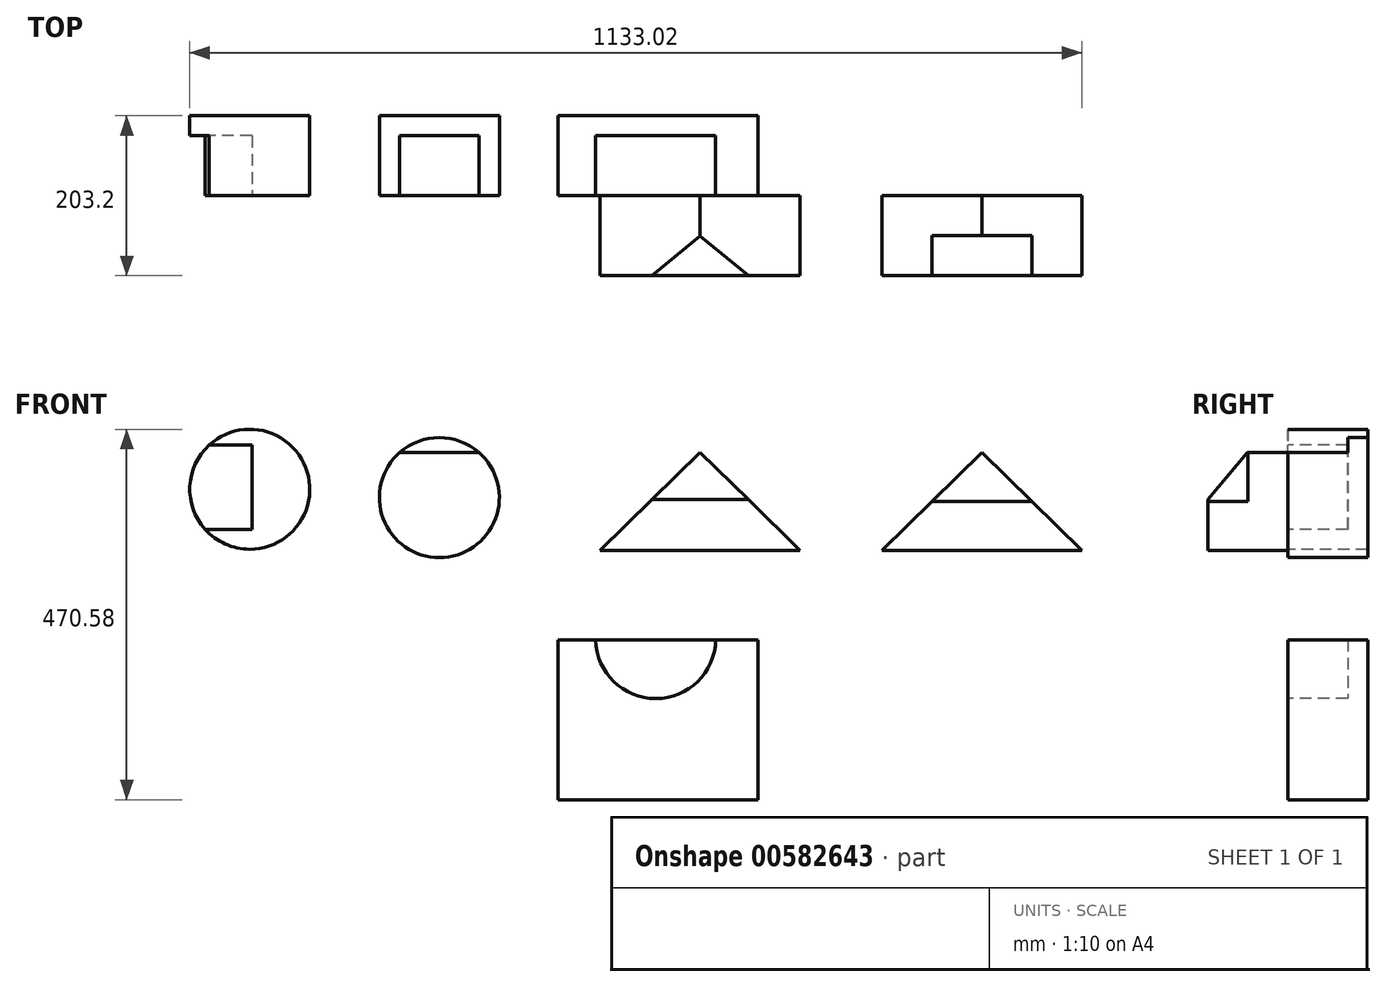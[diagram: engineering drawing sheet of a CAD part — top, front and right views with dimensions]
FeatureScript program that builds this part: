
annotation { "Feature Type Name" : "Feature", "Feature Type Description" : "" }
export const myFeature = defineFeature(function(context is Context, id is Id, definition is map)
    precondition{}
    {
        {
            var Q0;
            Q0=qCreatedBy(makeId("Front.planeOp"),FACE);
            var sketch = newSketch(context, id + "F0", { "sketchPlane" : qUnion([Q0])});
            skLineSegment(sketch, "E0", {"start": v(0, 0) * mm, "end": v(254, 0) * mm});
            skLineSegment(sketch, "E1", {"start": v(254, 0) * mm, "end": v(127, 124.43) * mm});
            skLineSegment(sketch, "E2", {"start": v(127, 124.43) * mm, "end": v(0, 0) * mm});
            skLineSegment(sketch, "E3", {"start": v(190.5, 62.22) * mm, "end": v(63.5, 62.22) * mm});
            skSolve(sketch);
        }
        {
            var Q0;
            {var subQ0=sQuery(id+"F0.wireOp",EDGE,"E0");Q0=makeQuery(id+"F0.imprint","IMPRINT",FACE,{"disambiguationData":[TD([[makeQuery(id+"F0.imprint","IMPRINT",EDGE,{"derivedFrom":subQ0}),1.0]])]});}
            extrude(context, id + "F1", {"entities" : qUnion([Q0]), "depth" : 101.6 * mm, "offsetDistance" : 25.4 * mm});
        }
        {
            var Q0;
            Q0 = qSketchRegion(id + "F0", true);
            extrude(context, id + "F2", {"entities" : qUnion([Q0]), "operationType" : NewBodyOperationType.ADD, "depth" : 50.8 * mm, "offsetDistance" : 25.4 * mm});
        }
        {
            var Q0;
            Q0=qCreatedBy(makeId("Front.planeOp"),FACE);
            var sketch = newSketch(context, id + "F3", { "sketchPlane" : qUnion([Q0])});
            skLineSegment(sketch, "E4", {"start": v(-103.68, 0) * mm, "end": v(-357.68, 0) * mm});
            skLineSegment(sketch, "E5", {"start": v(-357.68, 0) * mm, "end": v(-230.68, 124.43) * mm});
            skLineSegment(sketch, "E6", {"start": v(-230.68, 124.43) * mm, "end": v(-103.68, 0) * mm});
            skSolve(sketch);
        }
        {
            var Q0;
            Q0=makeQuery(id+"F3.imprint","IMPRINT",FACE,{"disambiguationData":[TD([[makeQuery(id+"F3.imprint","IMPRINT",EDGE,{"derivedFrom":sQuery(id+"F3.wireOp",EDGE,"E4")}),-1.0]])]});
            extrude(context, id + "F4", {"entities" : qUnion([Q0]), "depth" : 101.6 * mm, "offsetDistance" : 25.4 * mm});
        }
        {
            var Q0;
            Q0=makeQuery(id+"F4.opExtrude","CAP_EDGE",EDGE,{"disambiguationData":[OSD([sQuery(id+"F3.wireOp",EDGE,"E4")])],"isStart":false});
            cPoint(context, id + "F5", {"entities" : qUnion([Q0]), "parameter" : 0.5});
        }
        {
            var Q0;
            Q0=makeQuery(id+"F4.opExtrude","CAP_VERTEX",VERTEX,{"disambiguationData":[OSD([sQuery(id+"F3.wireOp",EDGE,"E5"),sQuery(id+"F3.wireOp",EDGE,"E6")])],"isStart":false});
            var Q1;
            Q1=makeQuery(id+"F4.opExtrude","CAP_VERTEX",VERTEX,{"disambiguationData":[OSD([sQuery(id+"F3.wireOp",EDGE,"E5"),sQuery(id+"F3.wireOp",EDGE,"E6")])],"isStart":true});
            var Q2;
            Q2 = qCreatedBy(id + "F5" ,VERTEX);
            cPlane(context, id + "F6", {"entities" : qUnion([Q0, Q1, Q2]), "cplaneType" : CPlaneType.THREE_POINT, "offset" : 25.4 * mm, "width" : 152.4 * mm, "height" : 152.4 * mm});
        }
        {
            var Q0;
            Q0=qCreatedBy(id+"F6.planeOp",FACE);
            var sketch = newSketch(context, id + "F7", { "sketchPlane" : qUnion([Q0])});
            skLineSegment(sketch, "E7", {"start": v(-51.02, 124.47) * mm, "end": v(-101.82, 124.47) * mm});
            skLineSegment(sketch, "E8", {"start": v(-101.82, 124.47) * mm, "end": v(-101.82, 64.04) * mm});
            skLineSegment(sketch, "E9", {"start": v(-101.82, 64.04) * mm, "end": v(-51.02, 124.47) * mm});
            skSolve(sketch);
        }
        {
            var Q0;
            Q0 = qSketchRegion(id + "F7", true);
            extrude(context, id + "F8", {"entities" : qUnion([Q0]), "operationType" : NewBodyOperationType.REMOVE, "endBound" : BoundingType.SYMMETRIC, "depth" : 127 * mm, "offsetDistance" : 25.4 * mm});
        }
        {
            var Q0;
            Q0=qCreatedBy(makeId("Front.planeOp"),FACE);
            var sketch = newSketch(context, id + "F9", { "sketchPlane" : qUnion([Q0])});
            skCircle(sketch, "E10", {"center": v(-562.02, 67) * mm, "radius": 76.2 * mm});
            skSolve(sketch);
        }
        {
            var Q0;
            Q0=makeQuery(id+"F9.imprint","IMPRINT",FACE,{"disambiguationData":[TD([[makeQuery(id+"F9.imprint","IMPRINT",EDGE,{"derivedFrom":sQuery(id+"F9.wireOp",EDGE,"E10")}),1.0]])]});
            extrude(context, id + "F10", {"entities" : qUnion([Q0]), "oppositeDirection" : true, "depth" : 101.6 * mm, "offsetDistance" : 25.4 * mm});
        }
        {
            var Q0;
            Q0=qCreatedBy(makeId("Front.planeOp"),FACE);
            var sketch = newSketch(context, id + "F11", { "sketchPlane" : qUnion([Q0])});
            skLineSegment(sketch, "E11.bottom", {"start": v(-493.99, 124.3) * mm, "end": v(-632.83, 124.3) * mm});
            skLineSegment(sketch, "E11.top", {"start": v(-493.99, 197.23) * mm, "end": v(-632.83, 197.23) * mm});
            skLineSegment(sketch, "E11.left", {"start": v(-493.99, 124.3) * mm, "end": v(-493.99, 197.23) * mm});
            skLineSegment(sketch, "E11.right", {"start": v(-632.83, 124.3) * mm, "end": v(-632.83, 197.23) * mm});
            skPoint(sketch, "E11.middle", {"position": v(-563.41, 160.77) * mm});
            skSolve(sketch);
        }
        {
            var Q0;
            Q0=makeQuery(id+"F11.imprint","IMPRINT",FACE,{"disambiguationData":[TD([[makeQuery(id+"F11.imprint","IMPRINT",EDGE,{"derivedFrom":sQuery(id+"F11.wireOp",EDGE,"E11.bottom")}),-1.0]])]});
            extrude(context, id + "F12", {"entities" : qUnion([Q0]), "operationType" : NewBodyOperationType.REMOVE, "oppositeDirection" : true, "depth" : 76.2 * mm, "offsetDistance" : 25.4 * mm});
        }
        {
            var Q0;
            Q0=qCreatedBy(makeId("Front.planeOp"),FACE);
            var sketch = newSketch(context, id + "F13", { "sketchPlane" : qUnion([Q0])});
            skCircle(sketch, "E12", {"center": v(-802.82, 77.57) * mm, "radius": 76.2 * mm});
            skSolve(sketch);
        }
        {
            var Q0;
            Q0=makeQuery(id+"F13.imprint","IMPRINT",FACE,{"disambiguationData":[TD([[makeQuery(id+"F13.imprint","IMPRINT",EDGE,{"derivedFrom":sQuery(id+"F13.wireOp",EDGE,"E12")}),1.0]])]});
            extrude(context, id + "F14", {"entities" : qUnion([Q0]), "oppositeDirection" : true, "depth" : 101.6 * mm, "offsetDistance" : 25.4 * mm});
        }
        {
            var Q0;
            Q0=qCreatedBy(makeId("Front.planeOp"),FACE);
            var sketch = newSketch(context, id + "F15", { "sketchPlane" : qUnion([Q0])});
            skLineSegment(sketch, "E13.bottom", {"start": v(-800.04, 26.76) * mm, "end": v(-960.33, 26.76) * mm});
            skLineSegment(sketch, "E13.top", {"start": v(-800.04, 133.62) * mm, "end": v(-960.33, 133.62) * mm});
            skLineSegment(sketch, "E13.left", {"start": v(-800.04, 26.76) * mm, "end": v(-800.04, 133.62) * mm});
            skLineSegment(sketch, "E13.right", {"start": v(-960.33, 26.76) * mm, "end": v(-960.33, 133.62) * mm});
            skPoint(sketch, "E13.middle", {"position": v(-880.18, 80.2) * mm});
            skSolve(sketch);
        }
        {
            var Q0;
            Q0=makeQuery(id+"F15.imprint","IMPRINT",FACE,{"disambiguationData":[TD([[makeQuery(id+"F15.imprint","IMPRINT",EDGE,{"derivedFrom":sQuery(id+"F15.wireOp",EDGE,"E13.bottom")}),-1.0]])]});
            extrude(context, id + "F16", {"entities" : qUnion([Q0]), "operationType" : NewBodyOperationType.REMOVE, "oppositeDirection" : true, "depth" : 76.2 * mm, "offsetDistance" : 25.4 * mm});
        }
        {
            var Q0;
            Q0=qCreatedBy(makeId("Front.planeOp"),FACE);
            var sketch = newSketch(context, id + "F17", { "sketchPlane" : qUnion([Q0])});
            skLineSegment(sketch, "E14.bottom", {"start": v(-157.26, -316.81) * mm, "end": v(-411.26, -316.81) * mm});
            skLineSegment(sketch, "E14.top", {"start": v(-157.26, -113.61) * mm, "end": v(-411.26, -113.61) * mm});
            skLineSegment(sketch, "E14.left", {"start": v(-157.26, -316.81) * mm, "end": v(-157.26, -113.61) * mm});
            skLineSegment(sketch, "E14.right", {"start": v(-411.26, -316.81) * mm, "end": v(-411.26, -113.61) * mm});
            skPoint(sketch, "E14.middle", {"position": v(-284.26, -215.21) * mm});
            skSolve(sketch);
        }
        {
            var Q0;
            Q0=makeQuery(id+"F17.imprint","IMPRINT",FACE,{"disambiguationData":[TD([[makeQuery(id+"F17.imprint","IMPRINT",EDGE,{"derivedFrom":sQuery(id+"F17.wireOp",EDGE,"E14.bottom")}),-1.0]])]});
            extrude(context, id + "F18", {"entities" : qUnion([Q0]), "oppositeDirection" : true, "depth" : 101.6 * mm, "offsetDistance" : 25.4 * mm});
        }
        {
            var Q0;
            Q0=qCreatedBy(makeId("Front.planeOp"),FACE);
            var sketch = newSketch(context, id + "F19", { "sketchPlane" : qUnion([Q0])});
            skCircle(sketch, "E15", {"center": v(-287.13, -112.24) * mm, "radius": 76.2 * mm});
            skSolve(sketch);
        }
        {
            var Q0;
            Q0=makeQuery(id+"F19.imprint","IMPRINT",FACE,{"disambiguationData":[TD([[makeQuery(id+"F19.imprint","IMPRINT",EDGE,{"derivedFrom":sQuery(id+"F19.wireOp",EDGE,"E15")}),1.0]])]});
            extrude(context, id + "F20", {"entities" : qUnion([Q0]), "operationType" : NewBodyOperationType.REMOVE, "oppositeDirection" : true, "depth" : 76.2 * mm, "offsetDistance" : 25.4 * mm});
        }
    });
